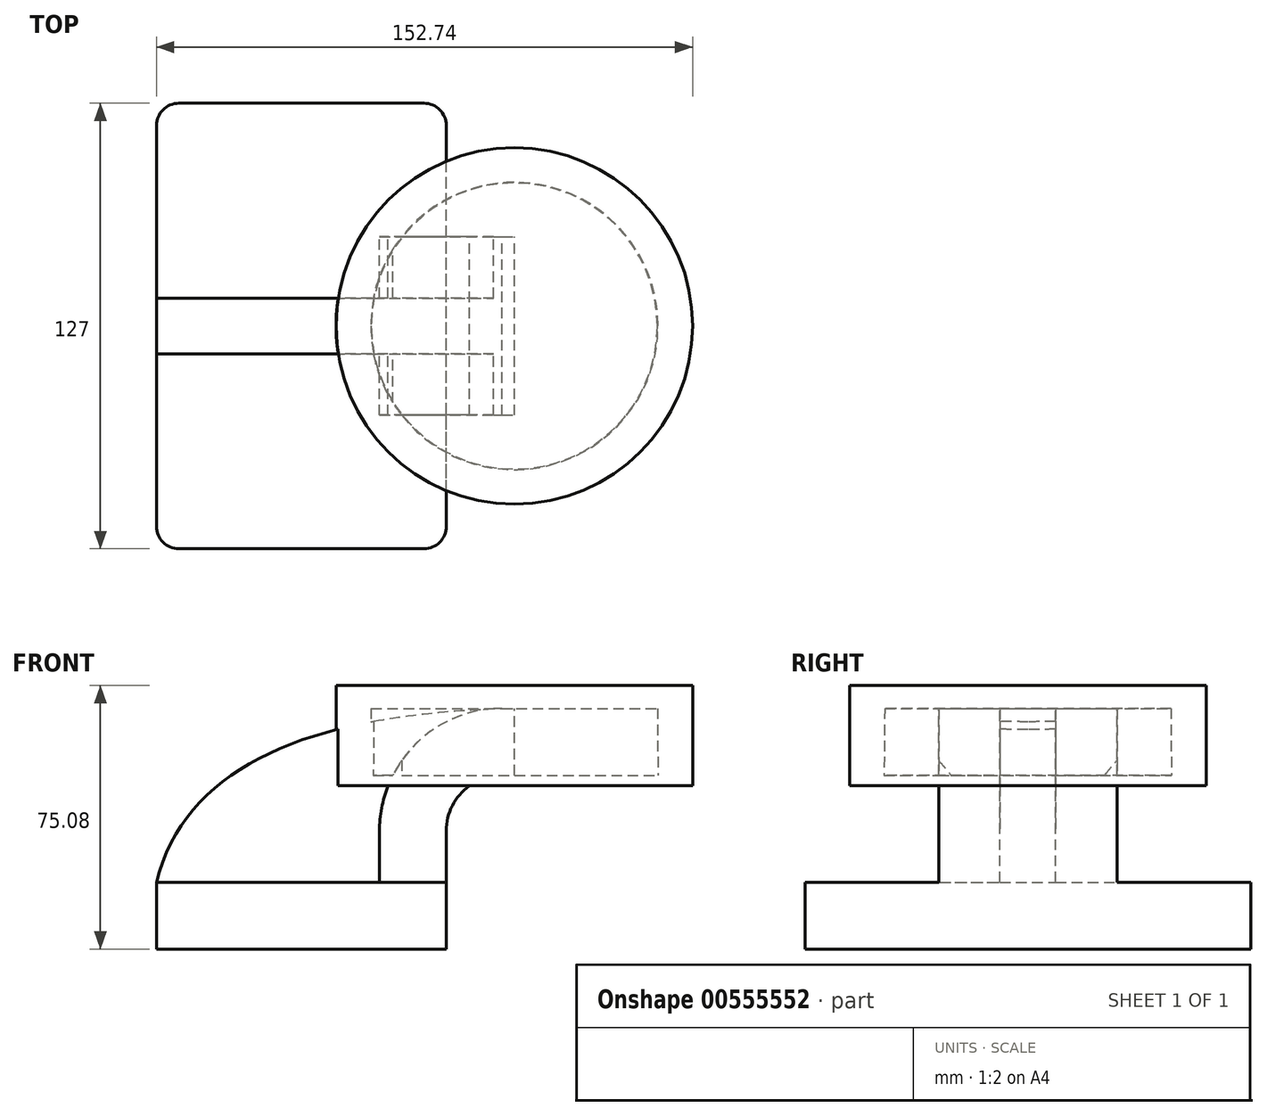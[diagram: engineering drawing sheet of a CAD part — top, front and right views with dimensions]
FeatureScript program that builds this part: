
annotation { "Feature Type Name" : "Feature", "Feature Type Description" : "" }
export const myFeature = defineFeature(function(context is Context, id is Id, definition is map)
    precondition{}
    {
        {
            var Q0;
            Q0=qCreatedBy(makeId("Front.planeOp"),FACE);
            var sketch = newSketch(context, id + "F0", { "sketchPlane" : qUnion([Q0])});
            skLineSegment(sketch, "E0.bottom", {"start": v(-41.28, 9.52) * mm, "end": v(41.28, 9.53) * mm});
            skLineSegment(sketch, "E0.top", {"start": v(-41.28, -9.53) * mm, "end": v(41.28, -9.53) * mm});
            skLineSegment(sketch, "E0.left", {"start": v(-41.28, 9.52) * mm, "end": v(-41.28, -9.53) * mm});
            skLineSegment(sketch, "E0.right", {"start": v(41.28, 9.53) * mm, "end": v(41.28, -9.52) * mm});
            skPoint(sketch, "E0.middle", {"position": v(0, 0) * mm});
            skLineSegment(sketch, "E1.bottom", {"start": v(111.46, 36.97) * mm, "end": v(60.66, 36.97) * mm});
            skLineSegment(sketch, "E1.top", {"start": v(111.46, 65.55) * mm, "end": v(60.66, 65.55) * mm});
            skLineSegment(sketch, "E1.left", {"start": v(111.46, 36.97) * mm, "end": v(111.46, 65.55) * mm});
            skLineSegment(sketch, "E1.right", {"start": v(60.66, 36.97) * mm, "end": v(60.66, 65.55) * mm});
            skPoint(sketch, "E1.middle", {"position": v(86.06, 51.26) * mm});
            skLineSegment(sketch, "E2", {"start": v(41.27, 9.53) * mm, "end": v(41.27, 24.1) * mm});
            skArc(sketch, "E3", {"start": v(57.15, 39.98) * mm, "mid": v(45.92, 35.33) * mm, "end": v(41.27, 24.1) * mm});
            skLineSegment(sketch, "E4", {"start": v(57.15, 39.98) * mm, "end": v(101.6, 39.98) * mm});
            skLineSegment(sketch, "E5.0", {"start": v(57.15, 59.03) * mm, "end": v(101.43, 59.03) * mm});
            skArc(sketch, "E5.1", {"start": v(57.15, 59.03) * mm, "mid": v(32.45, 48.8) * mm, "end": v(22.23, 24.1) * mm});
            skLineSegment(sketch, "E5.2", {"start": v(22.22, 9.53) * mm, "end": v(22.22, 24.1) * mm});
            skLineSegment(sketch, "E6", {"start": v(101.6, 39.98) * mm, "end": v(101.43, 59.03) * mm});
            skFitSpline(sketch, "E7", {"points": [v(-41.28, 9.52) * mm, v(57.15, 59.03) * mm], "startDerivative": vector(24.84, 102.4) * mm, "endDerivative": vector(157.55, 4.81) * mm});
            skSolve(sketch);
        }
        {
            var Q0;
            Q0=makeQuery(id+"F0.imprint","IMPRINT",FACE,{"disambiguationData":[TD([[makeQuery(id+"F0.imprint","IMPRINT",EDGE,{"derivedFrom":sQuery(id+"F0.wireOp",EDGE,"E0.top")}),1.0]])]});
            extrude(context, id + "F1", {"entities" : qUnion([Q0]), "endBound" : BoundingType.SYMMETRIC, "depth" : 127 * mm, "offsetDistance" : 25.4 * mm});
        }
        {
            var Q0;
            {var subQ1=sQuery(id+"F0.wireOp",EDGE,"E2");Q0=makeQuery(id+"F0.imprint","IMPRINT",FACE,{"disambiguationData":[TD([[makeQuery(id+"F0.imprint","IMPRINT",EDGE,{"derivedFrom":subQ1}),1.0]])]});}
            extrude(context, id + "F2", {"entities" : qUnion([Q0]), "operationType" : NewBodyOperationType.ADD, "endBound" : BoundingType.SYMMETRIC, "depth" : 50.8 * mm, "offsetDistance" : 25.4 * mm});
        }
        {
            var Q0;
            {var subQ3=sQuery(id+"F0.wireOp",EDGE,"E5.2");Q0=makeQuery(id+"F0.imprint","IMPRINT",FACE,{"disambiguationData":[TD([[makeQuery(id+"F0.imprint","IMPRINT",EDGE,{"derivedFrom":subQ3}),1.0]])]});}
            extrude(context, id + "F3", {"entities" : qUnion([Q0]), "operationType" : NewBodyOperationType.ADD, "endBound" : BoundingType.SYMMETRIC, "depth" : 15.88 * mm, "offsetDistance" : 25.4 * mm});
        }
        {
            var Q0;
            {var subQ1=sQuery(id+"F0.wireOp",EDGE,"E1.bottom");Q0=makeQuery(id+"F0.imprint","IMPRINT",FACE,{"disambiguationData":[TD([[makeQuery(id+"F0.imprint","IMPRINT",EDGE,{"derivedFrom":subQ1}),-1.0]])]});}
            var Q1;
            Q1=sQuery(id+"F0.wireOp",EDGE,"E1.right");
            revolve(context, id + "F4", {"operationType" : NewBodyOperationType.ADD, "entities" : qUnion([Q0]), "axis" : qUnion([Q1]), "revolveType" : RevolveType.FULL});
        }
        {
            var Q0;
            Q0=makeQuery(id+"F1.opExtrude","CAP_EDGE",EDGE,{"disambiguationData":[OSD([sQuery(id+"F0.wireOp",EDGE,"E0.right")])],"isStart":false});
            var Q1;
            Q1=makeQuery(id+"F1.opExtrude","CAP_EDGE",EDGE,{"disambiguationData":[OSD([sQuery(id+"F0.wireOp",EDGE,"E0.left")])],"isStart":false});
            var Q2;
            Q2=makeQuery(id+"F1.opExtrude","CAP_EDGE",EDGE,{"disambiguationData":[OSD([sQuery(id+"F0.wireOp",EDGE,"E0.right")])],"isStart":true});
            var Q3;
            Q3=makeQuery(id+"F1.opExtrude","CAP_EDGE",EDGE,{"disambiguationData":[OSD([sQuery(id+"F0.wireOp",EDGE,"E0.left")])],"isStart":true});
            fillet(context, id + "F5", {"entities" : qUnion([Q0, Q1, Q2, Q3]), "radius" : 6.35 * mm, "tangentPropagation" : true, "allowEdgeOverflow" : false});
        }
    });
